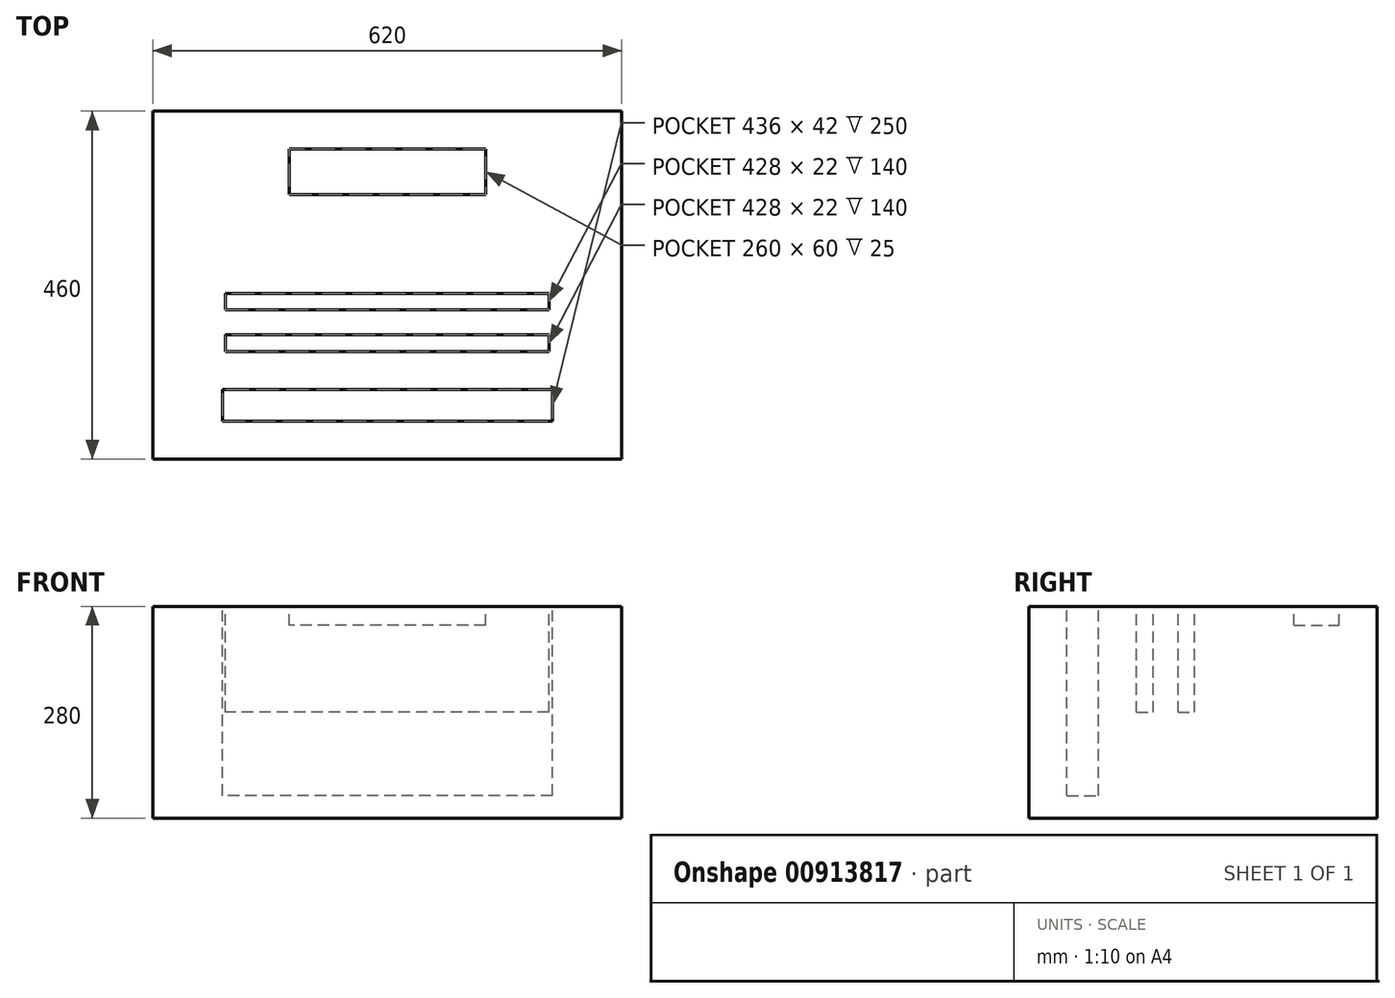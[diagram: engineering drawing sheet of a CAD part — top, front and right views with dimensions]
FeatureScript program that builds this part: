
annotation { "Feature Type Name" : "Feature", "Feature Type Description" : "" }
export const myFeature = defineFeature(function(context is Context, id is Id, definition is map)
    precondition{}
    {
        {
            var Q0;
            Q0=qCreatedBy(makeId("Top.planeOp"),FACE);
            var sketch = newSketch(context, id + "F0", { "sketchPlane" : qUnion([Q0])});
            skLineSegment(sketch, "E0.bottom", {"start": v(310.34, -142) * mm, "end": v(-309.66, -142) * mm});
            skLineSegment(sketch, "E0.top", {"start": v(310.34, 318) * mm, "end": v(-309.66, 318) * mm});
            skLineSegment(sketch, "E0.left", {"start": v(310.34, -142) * mm, "end": v(310.34, 318) * mm});
            skLineSegment(sketch, "E0.right", {"start": v(-309.66, -142) * mm, "end": v(-309.66, 318) * mm});
            skLineSegment(sketch, "E1.bottom", {"start": v(218.34, -92) * mm, "end": v(-217.66, -92) * mm});
            skLineSegment(sketch, "E1.top", {"start": v(218.34, -50) * mm, "end": v(-217.66, -50) * mm});
            skLineSegment(sketch, "E1.left", {"start": v(218.34, -92) * mm, "end": v(218.34, -50) * mm});
            skLineSegment(sketch, "E1.right", {"start": v(-217.66, -92) * mm, "end": v(-217.66, -50) * mm});
            skPoint(sketch, "E1.middle", {"position": v(0, 0) * mm});
            skLineSegment(sketch, "E2.direction1", {"start": v(-217.66, -92) * mm, "end": v(-182.5, -92) * mm, "construction": true});
            skLineSegment(sketch, "E2.direction2", {"start": v(-217.66, -92) * mm, "end": v(-217.66, -20) * mm, "construction": true});
            skLineSegment(sketch, "E3.bottom", {"start": v(214, 0) * mm, "end": v(-214, 0) * mm});
            skLineSegment(sketch, "E3.top", {"start": v(214, 22) * mm, "end": v(-214, 22) * mm});
            skLineSegment(sketch, "E3.left", {"start": v(214, 0) * mm, "end": v(214, 22) * mm});
            skLineSegment(sketch, "E3.right", {"start": v(-214, 0) * mm, "end": v(-214, 22) * mm});
            skPoint(sketch, "E3.middle", {"position": v(0, 11) * mm});
            skLineSegment(sketch, "E4.0.1.0", {"start": v(-214, 55) * mm, "end": v(-214, 77) * mm});
            skLineSegment(sketch, "E4.0.1.1", {"start": v(214, 55) * mm, "end": v(-214, 55) * mm});
            skLineSegment(sketch, "E4.0.1.2", {"start": v(214, 77) * mm, "end": v(-214, 77) * mm});
            skLineSegment(sketch, "E4.0.1.3", {"start": v(214, 55) * mm, "end": v(214, 77) * mm});
            skLineSegment(sketch, "E4.direction1", {"start": v(-214, 0) * mm, "end": v(-189, 0) * mm, "construction": true});
            skLineSegment(sketch, "E4.direction2", {"start": v(-214, 0) * mm, "end": v(-214, 55) * mm, "construction": true});
            skSolve(sketch);
        }
        {
            var Q0;
            Q0=makeQuery(id+"F0.imprint","IMPRINT",FACE,{"disambiguationData":[TD([[makeQuery(id+"F0.imprint","IMPRINT",EDGE,{"derivedFrom":sQuery(id+"F0.wireOp",EDGE,"E0.bottom")}),-1.0]])]});
            var Q1;
            Q1=makeQuery(id+"F0.imprint","IMPRINT",FACE,{"disambiguationData":[TD([[makeQuery(id+"F0.imprint","IMPRINT",EDGE,{"derivedFrom":sQuery(id+"F0.wireOp",EDGE,"E2.0.2.0")}),1.0]])]});
            var Q2;
            Q2=makeQuery(id+"F0.imprint","IMPRINT",FACE,{"disambiguationData":[TD([[makeQuery(id+"F0.imprint","IMPRINT",EDGE,{"derivedFrom":sQuery(id+"F0.wireOp",EDGE,"E2.0.1.0")}),1.0]])]});
            var Q3;
            Q3=makeQuery(id+"F0.imprint","IMPRINT",FACE,{"disambiguationData":[TD([[makeQuery(id+"F0.imprint","IMPRINT",EDGE,{"derivedFrom":sQuery(id+"F0.wireOp",EDGE,"E1.bottom")}),-1.0]])]});
            var Q4;
            Q4=makeQuery(id+"F0.imprint","IMPRINT",FACE,{"disambiguationData":[TD([[makeQuery(id+"F0.imprint","IMPRINT",EDGE,{"derivedFrom":sQuery(id+"F0.wireOp",EDGE,"E3.bottom")}),-1.0]])]});
            var Q5;
            Q5=makeQuery(id+"F0.imprint","IMPRINT",FACE,{"disambiguationData":[TD([[makeQuery(id+"F0.imprint","IMPRINT",EDGE,{"derivedFrom":sQuery(id+"F0.wireOp",EDGE,"E4.0.1.0")}),-1.0]])]});
            var Q6;
            Q6=makeQuery(id+"F0.imprint","IMPRINT",FACE,{"disambiguationData":[TD([[makeQuery(id+"F0.imprint","IMPRINT",EDGE,{"derivedFrom":sQuery(id+"F0.wireOp",EDGE,"E4.0.2.0")}),-1.0]])]});
            var Q7;
            Q7=makeQuery(id+"F0.imprint","IMPRINT",FACE,{"disambiguationData":[TD([[makeQuery(id+"F0.imprint","IMPRINT",EDGE,{"derivedFrom":sQuery(id+"F0.wireOp",EDGE,"E4.0.3.0")}),-1.0]])]});
            var Q8;
            Q8=makeQuery(id+"F0.imprint","IMPRINT",FACE,{"disambiguationData":[TD([[makeQuery(id+"F0.imprint","IMPRINT",EDGE,{"derivedFrom":sQuery(id+"F0.wireOp",EDGE,"E4.0.4.0")}),-1.0]])]});
            var Q9;
            Q9=makeQuery(id+"F0.imprint","IMPRINT",FACE,{"disambiguationData":[TD([[makeQuery(id+"F0.imprint","IMPRINT",EDGE,{"derivedFrom":sQuery(id+"F0.wireOp",EDGE,"E4.0.5.0")}),-1.0]])]});
            extrude(context, id + "F1", {"entities" : qUnion([Q0, Q1, Q2, Q3, Q4, Q5, Q6, Q7, Q8, Q9]), "oppositeDirection" : true, "depth" : 280 * mm, "offsetDistance" : 25 * mm});
        }
        {
            var Q0;
            Q0=makeQuery(id+"F0.imprint","IMPRINT",FACE,{"disambiguationData":[TD([[makeQuery(id+"F0.imprint","IMPRINT",EDGE,{"derivedFrom":sQuery(id+"F0.wireOp",EDGE,"E2.0.1.0")}),1.0]])]});
            var Q1;
            Q1=makeQuery(id+"F0.imprint","IMPRINT",FACE,{"disambiguationData":[TD([[makeQuery(id+"F0.imprint","IMPRINT",EDGE,{"derivedFrom":sQuery(id+"F0.wireOp",EDGE,"E1.bottom")}),-1.0]])]});
            extrude(context, id + "F2", {"entities" : qUnion([Q0, Q1]), "operationType" : NewBodyOperationType.REMOVE, "oppositeDirection" : true, "depth" : 250 * mm, "offsetDistance" : 25 * mm});
        }
        {
            var Q0;
            Q0=makeQuery(id+"F0.imprint","IMPRINT",FACE,{"disambiguationData":[TD([[makeQuery(id+"F0.imprint","IMPRINT",EDGE,{"derivedFrom":sQuery(id+"F0.wireOp",EDGE,"E3.bottom")}),-1.0]])]});
            var Q1;
            Q1=makeQuery(id+"F0.imprint","IMPRINT",FACE,{"disambiguationData":[TD([[makeQuery(id+"F0.imprint","IMPRINT",EDGE,{"derivedFrom":sQuery(id+"F0.wireOp",EDGE,"E4.0.1.0")}),-1.0]])]});
            var Q2;
            Q2=makeQuery(id+"F0.imprint","IMPRINT",FACE,{"disambiguationData":[TD([[makeQuery(id+"F0.imprint","IMPRINT",EDGE,{"derivedFrom":sQuery(id+"F0.wireOp",EDGE,"E4.0.2.0")}),-1.0]])]});
            var Q3;
            Q3=makeQuery(id+"F0.imprint","IMPRINT",FACE,{"disambiguationData":[TD([[makeQuery(id+"F0.imprint","IMPRINT",EDGE,{"derivedFrom":sQuery(id+"F0.wireOp",EDGE,"E4.0.3.0")}),-1.0]])]});
            var Q4;
            Q4=makeQuery(id+"F0.imprint","IMPRINT",FACE,{"disambiguationData":[TD([[makeQuery(id+"F0.imprint","IMPRINT",EDGE,{"derivedFrom":sQuery(id+"F0.wireOp",EDGE,"E4.0.4.0")}),-1.0]])]});
            var Q5;
            Q5=makeQuery(id+"F0.imprint","IMPRINT",FACE,{"disambiguationData":[TD([[makeQuery(id+"F0.imprint","IMPRINT",EDGE,{"derivedFrom":sQuery(id+"F0.wireOp",EDGE,"E4.0.5.0")}),-1.0]])]});
            extrude(context, id + "F3", {"entities" : qUnion([Q0, Q1, Q2, Q3, Q4, Q5]), "operationType" : NewBodyOperationType.REMOVE, "oppositeDirection" : true, "depth" : 140 * mm, "offsetDistance" : 25 * mm});
        }
        {
            var Q0;
            Q0=makeQuery(id+"F1.opExtrude","CAP_FACE",FACE,{"disambiguationData":[OSD([sQuery(id+"F0.wireOp",EDGE,"E0.bottom"),sQuery(id+"F0.wireOp",EDGE,"E0.top"),sQuery(id+"F0.wireOp",EDGE,"E0.left"),sQuery(id+"F0.wireOp",EDGE,"E0.right")])],"isStart":true});
            var sketch = newSketch(context, id + "F4", { "sketchPlane" : qUnion([Q0])});
            skLineSegment(sketch, "E5.bottom", {"start": v(130.34, 208) * mm, "end": v(-129.66, 208) * mm});
            skLineSegment(sketch, "E5.top", {"start": v(130.34, 268) * mm, "end": v(-129.66, 268) * mm});
            skLineSegment(sketch, "E5.left", {"start": v(130.34, 208) * mm, "end": v(130.34, 268) * mm});
            skLineSegment(sketch, "E5.right", {"start": v(-129.66, 208) * mm, "end": v(-129.66, 268) * mm});
            skPoint(sketch, "E5.middle", {"position": v(0.34, 238) * mm});
            skSolve(sketch);
        }
        {
            var Q0;
            Q0=makeQuery(id+"F4.imprint","IMPRINT",FACE,{"disambiguationData":[TD([[makeQuery(id+"F4.imprint","IMPRINT",EDGE,{"derivedFrom":sQuery(id+"F4.wireOp",EDGE,"E5.bottom")}),-1.0]])]});
            extrude(context, id + "F5", {"entities" : qUnion([Q0]), "operationType" : NewBodyOperationType.REMOVE, "oppositeDirection" : true, "depth" : 25 * mm, "offsetDistance" : 25 * mm});
        }
    });
